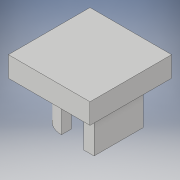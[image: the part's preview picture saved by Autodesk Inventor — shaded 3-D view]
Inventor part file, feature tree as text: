
AUTODESK INVENTOR PART (.ipt)
format: ipt  version: 2019 (Build 230136000, 136)  size: 118,784 bytes
history: native  units: mm
features: extrude x2, sketch x2
ambient origin geometry x8: Origin, YZ Plane, XZ Plane, XY Plane, X Axis, Y Axis, Z Axis, Center Point
bodies: Solid1 (feature_tree)
feature tree (4):
  extrude  "Extrusion1"  Depth=20.0mm
  extrude  "Extrusion2"  Depth=2.5mm
  sketch  "Sketch1"  dims[d0=20.0mm d1=20.0mm]
  sketch  "Sketch2"  dims[d2=5.0mm d3=0.0mm d6=2.5mm d7=2.5mm d9=3.0mm d11=12.0mm d13=3.0mm d14=3.0mm d15=2.5mm d16=10.0mm d17=0.0mm]
